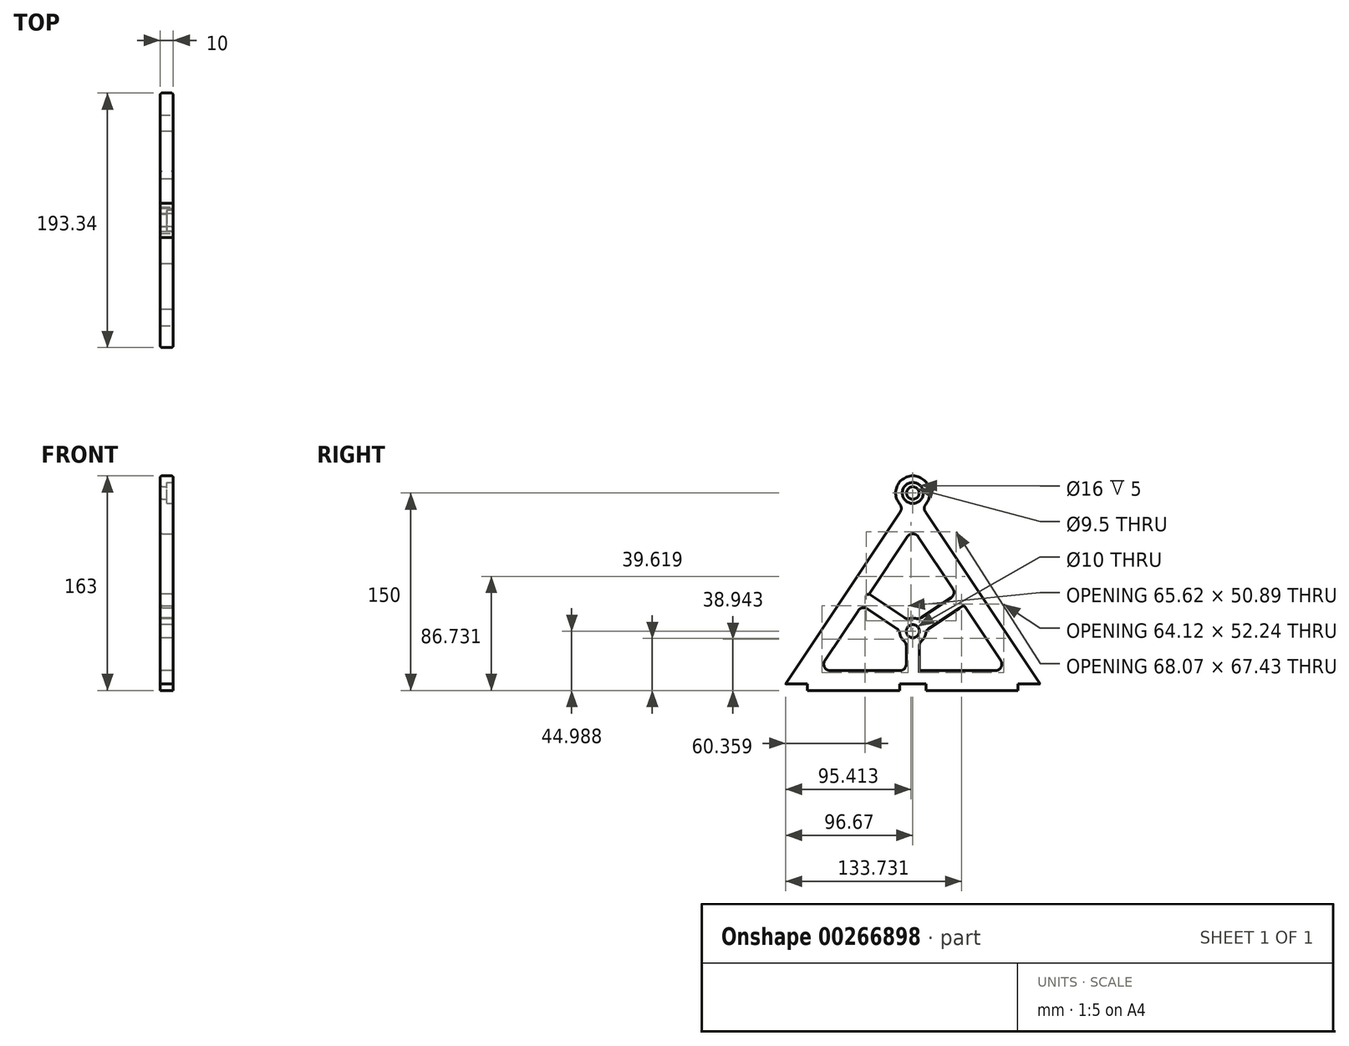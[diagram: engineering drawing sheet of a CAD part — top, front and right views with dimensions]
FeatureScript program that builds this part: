
annotation { "Feature Type Name" : "Feature", "Feature Type Description" : "" }
export const myFeature = defineFeature(function(context is Context, id is Id, definition is map)
    precondition{}
    {
        {
            var Q0;
            Q0=qCreatedBy(makeId("Right.planeOp"),FACE);
            var sketch = newSketch(context, id + "F0", { "sketchPlane" : qUnion([Q0])});
            skLineSegment(sketch, "E0", {"start": v(0, 0) * mm, "end": v(0, 150) * mm, "construction": true});
            skLineSegment(sketch, "E1", {"start": v(-100, 0) * mm, "end": v(100, 0) * mm});
            skLineSegment(sketch, "E2", {"start": v(-100, 0) * mm, "end": v(-7.21, 139.18) * mm});
            skLineSegment(sketch, "E3", {"start": v(100, 0) * mm, "end": v(7.21, 139.18) * mm});
            skCircle(sketch, "E4", {"center": v(0, 150) * mm, "radius": 8 * mm, "construction": true});
            skArc(sketch, "E5.0", {"start": v(7.21, 139.18) * mm, "mid": v(0, 163) * mm, "end": v(-7.21, 139.18) * mm});
            skLineSegment(sketch, "E6", {"start": v(-71.97, 15) * mm, "end": v(71.97, 15) * mm});
            skLineSegment(sketch, "E7", {"start": v(-71.97, 15) * mm, "end": v(0, 122.96) * mm});
            skLineSegment(sketch, "E8", {"start": v(0, 122.96) * mm, "end": v(71.97, 15) * mm});
            skSolve(sketch);
        }
        {
            var Q0;
            Q0 = qSketchRegion(id + "F0", true);
            extrude(context, id + "F1", {"entities" : qUnion([Q0]), "depth" : 10 * mm});
        }
        {
            var Q0;
            Q0=makeQuery(id+"F1.opExtrude","CAP_FACE",FACE,{"disambiguationData":[OSD([sQuery(id+"F0.wireOp",EDGE,"E1"),sQuery(id+"F0.wireOp",EDGE,"E2"),sQuery(id+"F0.wireOp",EDGE,"E3"),sQuery(id+"F0.wireOp",EDGE,"E5.0"),sQuery(id+"F0.wireOp",EDGE,"E6"),sQuery(id+"F0.wireOp",EDGE,"E7"),sQuery(id+"F0.wireOp",EDGE,"E8")])],"isStart":false});
            var sketch = newSketch(context, id + "F2", { "sketchPlane" : qUnion([Q0])});
            skCircle(sketch, "E9", {"center": v(0, 150) * mm, "radius": 8 * mm});
            skSolve(sketch);
        }
        {
            var Q0;
            Q0 = qSketchRegion(id + "F2", true);
            extrude(context, id + "F3", {"entities" : qUnion([Q0]), "operationType" : NewBodyOperationType.REMOVE, "oppositeDirection" : true, "depth" : 5 * mm});
        }
        {
            var Q0;
            Q0=makeQuery(id+"F3.boolean.opBoolean","COPY",FACE,{"derivedFrom":makeQuery(id+"F3.opExtrude","CAP_FACE",FACE,{"disambiguationData":[OSD([sQuery(id+"F2.wireOp",EDGE,"E9")])],"isStart":false})});
            var sketch = newSketch(context, id + "F4", { "sketchPlane" : qUnion([Q0])});
            skCircle(sketch, "E10", {"center": v(0, 150) * mm, "radius": 4.75 * mm});
            skSolve(sketch);
        }
        {
            var Q0;
            Q0 = qSketchRegion(id + "F4", true);
            extrude(context, id + "F5", {"entities" : qUnion([Q0]), "operationType" : NewBodyOperationType.REMOVE, "endBound" : BoundingType.THROUGH_ALL, "oppositeDirection" : true, "depth" : 25 * mm});
        }
        {
            var Q0;
            Q0=makeQuery(id+"F1.opExtrude","CAP_FACE",FACE,{"disambiguationData":[OSD([sQuery(id+"F0.wireOp",EDGE,"E1"),sQuery(id+"F0.wireOp",EDGE,"E2"),sQuery(id+"F0.wireOp",EDGE,"E3"),sQuery(id+"F0.wireOp",EDGE,"E5.0"),sQuery(id+"F0.wireOp",EDGE,"E6"),sQuery(id+"F0.wireOp",EDGE,"E7"),sQuery(id+"F0.wireOp",EDGE,"E8")])],"isStart":false});
            var sketch = newSketch(context, id + "F6", { "sketchPlane" : qUnion([Q0])});
            skLineSegment(sketch, "E11.bottom", {"start": v(-10, 0) * mm, "end": v(10, 0) * mm});
            skLineSegment(sketch, "E11.top", {"start": v(-10, 5) * mm, "end": v(10, 5) * mm});
            skLineSegment(sketch, "E11.left", {"start": v(-10, 0) * mm, "end": v(-10, 5) * mm});
            skLineSegment(sketch, "E11.right", {"start": v(10, 0) * mm, "end": v(10, 5) * mm});
            skLineSegment(sketch, "E12.bottom", {"start": v(100, 0) * mm, "end": v(80, 0) * mm});
            skLineSegment(sketch, "E12.top", {"start": v(100, 5) * mm, "end": v(80, 5) * mm});
            skLineSegment(sketch, "E12.left", {"start": v(100, 0) * mm, "end": v(100, 5) * mm});
            skLineSegment(sketch, "E12.right", {"start": v(80, 0) * mm, "end": v(80, 5) * mm});
            skLineSegment(sketch, "E13.bottom", {"start": v(-100, 0) * mm, "end": v(-80, 0) * mm});
            skLineSegment(sketch, "E13.top", {"start": v(-100, 5) * mm, "end": v(-80, 5) * mm});
            skLineSegment(sketch, "E13.left", {"start": v(-100, 0) * mm, "end": v(-100, 5) * mm});
            skLineSegment(sketch, "E13.right", {"start": v(-80, 0) * mm, "end": v(-80, 5) * mm});
            skSolve(sketch);
        }
        {
            var Q0;
            Q0 = qSketchRegion(id + "F6", true);
            extrude(context, id + "F7", {"entities" : qUnion([Q0]), "operationType" : NewBodyOperationType.REMOVE, "endBound" : BoundingType.THROUGH_ALL, "oppositeDirection" : true, "depth" : 25 * mm});
        }
        {
            var Q0;
            Q0=qCreatedBy(makeId("Right.planeOp"),FACE);
            var sketch = newSketch(context, id + "F8", { "sketchPlane" : qUnion([Q0])});
            skLineSegment(sketch, "E14", {"start": v(-35.99, 68.98) * mm, "end": v(0, 44.99) * mm, "construction": true});
            skLineSegment(sketch, "E15", {"start": v(0, 44.99) * mm, "end": v(35.99, 68.98) * mm, "construction": true});
            skLineSegment(sketch, "E16", {"start": v(0, 44.99) * mm, "end": v(0, 15) * mm, "construction": true});
            skCircle(sketch, "E17", {"center": v(0, 44.99) * mm, "radius": 5 * mm});
            skArc(sketch, "E18.0", {"start": v(4.43, 53.95) * mm, "mid": v(0, 54.99) * mm, "end": v(-4.43, 53.95) * mm});
            skLineSegment(sketch, "E19.0", {"start": v(-38.76, 64.82) * mm, "end": v(-9.98, 45.63) * mm});
            skLineSegment(sketch, "E20.0", {"start": v(-33.21, 73.14) * mm, "end": v(-4.43, 53.95) * mm});
            skLineSegment(sketch, "E21.0", {"start": v(9.98, 45.63) * mm, "end": v(38.76, 64.82) * mm});
            skLineSegment(sketch, "E22.0", {"start": v(4.43, 53.95) * mm, "end": v(33.21, 73.14) * mm});
            skLineSegment(sketch, "E23.0", {"start": v(-5, 36.33) * mm, "end": v(-5, 15) * mm});
            skLineSegment(sketch, "E24", {"start": v(-38.76, 64.82) * mm, "end": v(-33.21, 73.14) * mm});
            skLineSegment(sketch, "E25", {"start": v(33.21, 73.14) * mm, "end": v(38.76, 64.82) * mm});
            skLineSegment(sketch, "E26", {"start": v(5, 15) * mm, "end": v(-5, 15) * mm});
            skArc(sketch, "E27.trimOffspring", {"start": v(-9.98, 45.63) * mm, "mid": v(-8.82, 40.27) * mm, "end": v(-5, 36.33) * mm});
            skArc(sketch, "E28.trimOffspring", {"start": v(5, 36.33) * mm, "mid": v(8.82, 40.27) * mm, "end": v(9.98, 45.63) * mm});
            skLineSegment(sketch, "E29.trimOffspring", {"start": v(5, 36.33) * mm, "end": v(5, 15) * mm});
            skSolve(sketch);
        }
        {
            var Q0;
            Q0 = qSketchRegion(id + "F8", true);
            extrude(context, id + "F9", {"entities" : qUnion([Q0]), "operationType" : NewBodyOperationType.ADD, "depth" : 10 * mm});
        }
        {
            var Q0;
            Q0=makeQuery(id+"F1.opExtrude","SWEPT_EDGE",EDGE,{"disambiguationData":[OSD([sQuery(id+"F0.wireOp",EDGE,"E2"),sQuery(id+"F0.wireOp",EDGE,"E5.0")])]});
            var Q1;
            Q1=makeQuery(id+"F1.opExtrude","SWEPT_EDGE",EDGE,{"disambiguationData":[OSD([sQuery(id+"F0.wireOp",EDGE,"E3"),sQuery(id+"F0.wireOp",EDGE,"E5.0")])]});
            var Q2;
            Q2=makeQuery(id+"F1.opExtrude","SWEPT_EDGE",EDGE,{"disambiguationData":[OSD([sQuery(id+"F0.wireOp",EDGE,"E6"),sQuery(id+"F0.wireOp",EDGE,"E8")])]});
            var Q3;
            Q3=makeQuery(id+"F1.opExtrude","SWEPT_EDGE",EDGE,{"disambiguationData":[OSD([sQuery(id+"F0.wireOp",EDGE,"E7"),sQuery(id+"F0.wireOp",EDGE,"E8")])]});
            var Q4;
            Q4=makeQuery(id+"F1.opExtrude","SWEPT_EDGE",EDGE,{"disambiguationData":[OSD([sQuery(id+"F0.wireOp",EDGE,"E6"),sQuery(id+"F0.wireOp",EDGE,"E7")])]});
            var Q5;
            Q5=makeQuery(id+"F9.opExtrude","SWEPT_EDGE",EDGE,{"disambiguationData":[OSD([sQuery(id+"F8.wireOp",EDGE,"E20.0"),sQuery(id+"F8.wireOp",EDGE,"E24")])]});
            var Q6;
            Q6=makeQuery(id+"F9.opExtrude","SWEPT_EDGE",EDGE,{"disambiguationData":[OSD([sQuery(id+"F8.wireOp",EDGE,"E19.0"),sQuery(id+"F8.wireOp",EDGE,"E24")])]});
            var Q7;
            Q7=makeQuery(id+"F9.opExtrude","SWEPT_EDGE",EDGE,{"disambiguationData":[OSD([sQuery(id+"F8.wireOp",EDGE,"E21.0"),sQuery(id+"F8.wireOp",EDGE,"E25")])]});
            var Q8;
            Q8=makeQuery(id+"F9.opExtrude","SWEPT_EDGE",EDGE,{"disambiguationData":[OSD([sQuery(id+"F8.wireOp",EDGE,"E19.0"),sQuery(id+"F8.wireOp",EDGE,"E27.trimOffspring")])]});
            var Q9;
            Q9=makeQuery(id+"F9.opExtrude","SWEPT_EDGE",EDGE,{"disambiguationData":[OSD([sQuery(id+"F8.wireOp",EDGE,"E23.0"),sQuery(id+"F8.wireOp",EDGE,"E27.trimOffspring")])]});
            var Q10;
            Q10=makeQuery(id+"F9.opExtrude","SWEPT_EDGE",EDGE,{"disambiguationData":[OSD([sQuery(id+"F8.wireOp",EDGE,"E28.trimOffspring"),sQuery(id+"F8.wireOp",EDGE,"E29.trimOffspring")])]});
            var Q11;
            Q11=makeQuery(id+"F9.opExtrude","SWEPT_EDGE",EDGE,{"disambiguationData":[OSD([sQuery(id+"F8.wireOp",EDGE,"E21.0"),sQuery(id+"F8.wireOp",EDGE,"E28.trimOffspring")])]});
            var Q12;
            Q12=makeQuery(id+"F9.opExtrude","SWEPT_EDGE",EDGE,{"disambiguationData":[OSD([sQuery(id+"F8.wireOp",EDGE,"E22.0"),sQuery(id+"F8.wireOp",EDGE,"E18.0")])]});
            var Q13;
            Q13=makeQuery(id+"F9.opExtrude","SWEPT_EDGE",EDGE,{"disambiguationData":[OSD([sQuery(id+"F8.wireOp",EDGE,"E20.0"),sQuery(id+"F8.wireOp",EDGE,"E18.0")])]});
            var Q14;
            Q14=makeQuery(id+"F9.opExtrude","SWEPT_EDGE",EDGE,{"disambiguationData":[OSD([sQuery(id+"F8.wireOp",EDGE,"E22.0"),sQuery(id+"F8.wireOp",EDGE,"E25")])]});
            var Q15;
            Q15=makeQuery(id+"F9.opExtrude","SWEPT_EDGE",EDGE,{"disambiguationData":[OSD([sQuery(id+"F8.wireOp",EDGE,"E23.0"),sQuery(id+"F8.wireOp",EDGE,"E26")])]});
            var Q16;
            Q16=makeQuery(id+"F9.opExtrude","SWEPT_EDGE",EDGE,{"disambiguationData":[OSD([sQuery(id+"F8.wireOp",EDGE,"E26"),sQuery(id+"F8.wireOp",EDGE,"E29.trimOffspring")])]});
            fillet(context, id + "F10", {"entities" : qUnion([Q0, Q1, Q2, Q3, Q4, Q5, Q6, Q7, Q8, Q9, Q10, Q11, Q12, Q13, Q14, Q15, Q16]), "radius" : 5 * mm, "tangentPropagation" : true, "allowEdgeOverflow" : false});
        }
        {
            var Q0;
            {var subQ13=sQuery(id+"F0.wireOp",EDGE,"E7");var subQ14=sQuery(id+"F0.wireOp",EDGE,"E8");Q0=makeQuery(id+"F9.boolean.opBoolean","SPLIT",FACE,{"disambiguationData":[TD([makeQuery(id+"F1.opExtrude","SWEPT_FACE",FACE,{"disambiguationData":[OSD([subQ13])]})])],"derivedFrom":makeQuery(id+"F1.opExtrude","SWEPT_FACE",FACE,{"disambiguationData":[OSD([subQ14])]})});}
            var Q1;
            {var subQ13=sQuery(id+"F0.wireOp",EDGE,"E8");var subQ15=sQuery(id+"F0.wireOp",EDGE,"E6");Q1=makeQuery(id+"F9.boolean.opBoolean","SPLIT",FACE,{"disambiguationData":[TD([makeQuery(id+"F1.opExtrude","SWEPT_FACE",FACE,{"disambiguationData":[OSD([subQ15])]})])],"derivedFrom":makeQuery(id+"F1.opExtrude","SWEPT_FACE",FACE,{"disambiguationData":[OSD([subQ13])]})});}
            var Q2;
            Q2=makeQuery(id+"F9.opExtrude","SWEPT_FACE",FACE,{"disambiguationData":[OSD([sQuery(id+"F8.wireOp",EDGE,"E19.0")])]});
            var Q3;
            Q3=makeQuery(id+"F9.opExtrude","SWEPT_FACE",FACE,{"disambiguationData":[OSD([sQuery(id+"F8.wireOp",EDGE,"E17")])]});
            var Q4;
            Q4=makeQuery(id+"F1.opExtrude","CAP_EDGE",EDGE,{"disambiguationData":[OSD([sQuery(id+"F0.wireOp",EDGE,"E2")])],"isStart":true});
            var Q5;
            Q5=makeQuery(id+"F1.opExtrude","CAP_EDGE",EDGE,{"disambiguationData":[OSD([sQuery(id+"F0.wireOp",EDGE,"E2")])],"isStart":false});
            var Q6;
            Q6=makeQuery(id+"F5.boolean.opBoolean","INTERSECT",EDGE,{"derivedFrom":[makeQuery(id+"F1.opExtrude","CAP_FACE",FACE,{"disambiguationData":[OSD([sQuery(id+"F0.wireOp",EDGE,"E1"),sQuery(id+"F0.wireOp",EDGE,"E2"),sQuery(id+"F0.wireOp",EDGE,"E3"),sQuery(id+"F0.wireOp",EDGE,"E5.0"),sQuery(id+"F0.wireOp",EDGE,"E6"),sQuery(id+"F0.wireOp",EDGE,"E7"),sQuery(id+"F0.wireOp",EDGE,"E8")])],"isStart":true}),makeQuery(id+"F5.opExtrude","SWEPT_FACE",FACE,{"disambiguationData":[OSD([sQuery(id+"F4.wireOp",EDGE,"E10")])]})]});
            fillet(context, id + "F11", {"entities" : qUnion([Q0, Q1, Q2, Q3, Q4, Q5, Q6]), "radius" : 1.5 * mm, "tangentPropagation" : true, "allowEdgeOverflow" : false});
        }
    });
